FCSTD DOCUMENT  (FreeCAD 1.0R39109 (Git))
Label: front
License: All rights reserved
LicenseURL: https://en.wikipedia.org/wiki/All_rights_reserved
objects: Sketcher::SketchObject×1, PartDesign::Body×1
note: 3 computed .brp shape members not serialized (recipe doc carries the construction recipe); baked Part::Feature solids carry a one-line shape summary decoded from their .brp

FEATURE [Sketcher::SketchObject] Sketch
  ArcFitTolerance = 1e-06
  AttachmentSupport = -> [XZ_Plane]
  FullyConstrained = false
  MakeInternals = false
  MapMode = 5
  Placement = pos=(0,0,0) rot=(1,0,0;1.5708rad)
  sketch-geometry (19):
    g0: LineSegment StartX=48.85 StartY=-19.1712 StartZ=0 EndX=86.85 EndY=-19.1712 EndZ=0
    g1: LineSegment StartX=91.05 StartY=-14.9712 StartZ=0 EndX=91.05 EndY=34.0288 EndZ=0
    g2: LineSegment StartX=86.85 StartY=38.2288 StartZ=0 EndX=48.85 EndY=38.2288 EndZ=0
    g3: LineSegment StartX=44.65 StartY=34.0288 StartZ=0 EndX=44.65 EndY=-14.9712 EndZ=0
    g4: ArcOfCircle CenterX=86.85 CenterY=34.0288 CenterZ=0 NormalX=0 NormalY=0 NormalZ=1 AngleXU=0 Radius=4.2 StartAngle=6e-16 EndAngle=1.5708
    g5: GeomPoint [constr] X=91.05 Y=38.2288 Z=0
    g6: ArcOfCircle CenterX=48.85 CenterY=34.0288 CenterZ=0 NormalX=0 NormalY=0 NormalZ=1 AngleXU=0 Radius=4.2 StartAngle=1.5708 EndAngle=3.14159
    g7: GeomPoint [constr] X=44.65 Y=38.2288 Z=0
    g8: ArcOfCircle CenterX=48.85 CenterY=-14.9712 CenterZ=0 NormalX=0 NormalY=0 NormalZ=1 AngleXU=0 Radius=4.2 StartAngle=3.14159 EndAngle=4.71239
    g9: GeomPoint [constr] X=44.65 Y=-19.1712 Z=0
    g10: ArcOfCircle CenterX=86.85 CenterY=-14.9712 CenterZ=0 NormalX=0 NormalY=0 NormalZ=1 AngleXU=0 Radius=4.2 StartAngle=4.71239 EndAngle=6.28319
    g11: GeomPoint [constr] X=91.05 Y=-19.1712 Z=0
    g12: Circle CenterX=0 CenterY=0 CenterZ=0 NormalX=0 NormalY=0 NormalZ=1 AngleXU=0 Radius=6.1
    g13: LineSegment StartX=35.85 StartY=39.2 StartZ=0 EndX=-35.85 EndY=39.2 EndZ=0
    g14: LineSegment StartX=-35.85 StartY=39.2 StartZ=0 EndX=-35.85 EndY=14.8 EndZ=0
    g15: LineSegment StartX=-35.85 StartY=14.8 StartZ=0 EndX=35.85 EndY=14.8 EndZ=0
    g16: LineSegment StartX=35.85 StartY=14.8 StartZ=0 EndX=35.85 EndY=39.2 EndZ=0
    g17: GeomPoint X=0 Y=14.8 Z=0
    g18: LineSegment [constr] StartX=0 StartY=14.8 StartZ=0 EndX=0 EndY=0 EndZ=0
  constraints (44):
    c: Horizontal(g0)
    c: Horizontal(g2)
    c: Vertical(g1)
    c: Vertical(g3)
    c: DistanceX(g7,g5) = 46.4
    c: DistanceY(g11,g5) = 57.4
    c: PointOnObject(g5,g2)
    c: PointOnObject(g5,g1)
    c: Tangent(g2,g4) = -1.5708
    c: Tangent(g1,g4) = -1.5708
    c: PointOnObject(g7,g2)
    c: PointOnObject(g7,g3)
    c: Tangent(g2,g6) = -1.5708
    c: Tangent(g3,g6) = -1.5708
    c: PointOnObject(g9,g0)
    c: PointOnObject(g9,g3)
    c: Tangent(g0,g8) = -1.5708
    c: Tangent(g3,g8) = -1.5708
    c: PointOnObject(g11,g0)
    c: PointOnObject(g11,g1)
    c: Tangent(g0,g10) = -1.5708
    c: Tangent(g1,g10) = -1.5708
    c: Radius(g4) = 4.2
    c: Equal(g4,g6)
    c: Equal(g10,g6)
    c: Equal(g8,g4)
    c: Coincident(g12,g-1)
    c: Diameter(g12) = 12.2
    c: Distance(g12,g3) = 38.55
    c: Coincident(g13,g14)
    c: Coincident(g14,g15)
    c: Coincident(g15,g16)
    c: Coincident(g16,g13)
    c: Horizontal(g13)
    c: Horizontal(g15)
    c: Vertical(g14)
    c: Vertical(g16)
    c: DistanceX(g13,g13) = 71.7
    c: DistanceY(g16,g16) = 24.4
    c: Symmetric(g15,g14,g17)
    c: Coincident(g18,g17)
    c: Coincident(g18,g12)
    c: Vertical(g18)
    c: DistanceY(g18,g18) = 14.8
FEATURE [PartDesign::Body] Body
  AllowCompound = false
  Group = -> [Sketch]
  Origin = -> Origin
